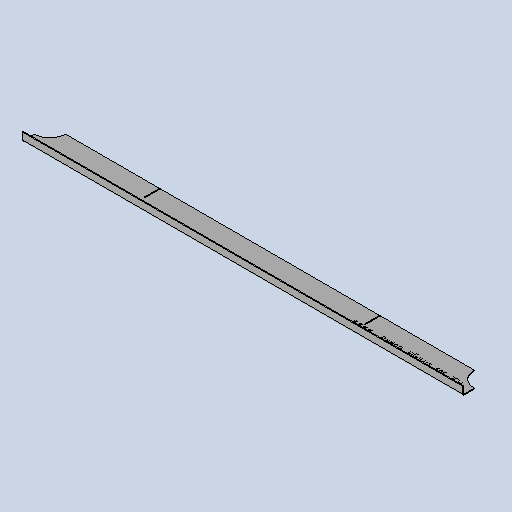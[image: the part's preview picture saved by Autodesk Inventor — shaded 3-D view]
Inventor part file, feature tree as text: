
AUTODESK INVENTOR PART (.ipt)
format: ipt  version: 2025 (Build 290162010, 162A)  size: 325,120 bytes
history: native  units: mm
features: other x5, sheet_metal_op x4, sketch x4, extrude x1
ambient origin geometry x8: Origin, YZ Plane, XZ Plane, XY Plane, X Axis, Y Axis, Z Axis, Center Point
bodies: Solid1 (feature_tree)
feature tree (14):
  sheet_metal_op  "Face1"
  sheet_metal_op  "Flange1"
  extrude  "Extrusion1"  Depth=62.0mm
  other  "Mark2"
  other  "A-Side Definition"
  sketch  "Sketch1"  dims[d0=980.0mm d1=62.0mm]
  other  "Plate1"
  sketch  "Sketch2"  dims[d2=2.0mm]
  other  "Plate2"
  sheet_metal_op  "Bend1"
  sheet_metal_op  "Corner1"
  sketch  "Sketch5"  dims[d3=2.0mm]
  sketch  "Sketch9"  dims[d4=1.0mm d5=4.0mm d6=2.75mm d7=20.0mm d8=90.0deg d9=2.75mm d10=8.0mm d11=2.0mm d12=2.75mm d15=0.0mm d16=0.0mm d40=200.0mm d41=12.0mm d45=70.0mm d48=2.1mm d49=490.0mm d51=29.0mm d52=33.0mm]
  other  "Definition1"
